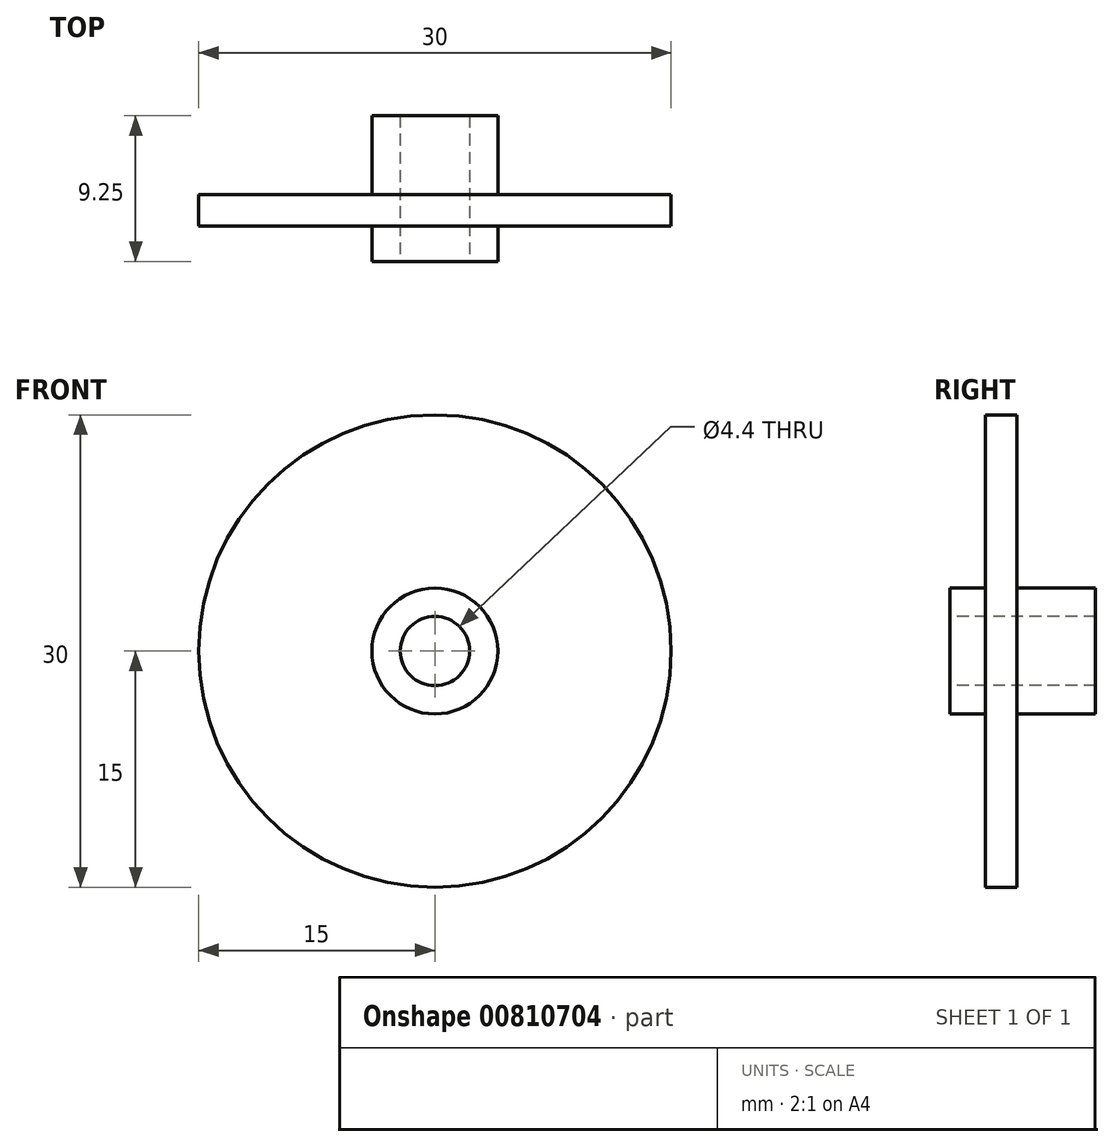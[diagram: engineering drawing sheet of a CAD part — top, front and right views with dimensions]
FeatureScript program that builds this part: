
annotation { "Feature Type Name" : "Feature", "Feature Type Description" : "" }
export const myFeature = defineFeature(function(context is Context, id is Id, definition is map)
    precondition{}
    {
        {
            var Q0;
            Q0=qCreatedBy(makeId("Front.planeOp"),FACE);
            var sketch = newSketch(context, id + "F0", { "sketchPlane" : qUnion([Q0])});
            skCircle(sketch, "E0", {"center": v(0, 0) * mm, "radius": 15 * mm});
            skSolve(sketch);
        }
        {
            var Q0;
            Q0=makeQuery(id+"F0.imprint","IMPRINT",FACE,{"disambiguationData":[TD([[makeQuery(id+"F0.imprint","IMPRINT",EDGE,{"derivedFrom":sQuery(id+"F0.wireOp",EDGE,"E0")}),1.0]])]});
            extrude(context, id + "F1", {"entities" : qUnion([Q0]), "depth" : 2 * mm, "offsetDistance" : 25 * mm});
        }
        {
            var Q0;
            Q0=makeQuery(id+"F1.opExtrude","CAP_FACE",FACE,{"disambiguationData":[OSD([sQuery(id+"F0.wireOp",EDGE,"E0")])],"isStart":false});
            var sketch = newSketch(context, id + "F2", { "sketchPlane" : qUnion([Q0])});
            skCircle(sketch, "E1", {"center": v(0, 0) * mm, "radius": 4 * mm});
            skSolve(sketch);
        }
        {
            var Q0;
            Q0=makeQuery(id+"F2.imprint","IMPRINT",FACE,{"disambiguationData":[TD([[makeQuery(id+"F2.imprint","IMPRINT",EDGE,{"derivedFrom":sQuery(id+"F2.wireOp",EDGE,"E1")}),1.0]])]});
            extrude(context, id + "F3", {"entities" : qUnion([Q0]), "operationType" : NewBodyOperationType.ADD, "depth" : 2.25 * mm, "offsetDistance" : 25 * mm});
        }
        {
            var Q0;
            Q0=makeQuery(id+"F3.opExtrude","CAP_FACE",FACE,{"disambiguationData":[OSD([sQuery(id+"F2.wireOp",EDGE,"E1")])],"isStart":false});
            var sketch = newSketch(context, id + "F4", { "sketchPlane" : qUnion([Q0])});
            skCircle(sketch, "E2", {"center": v(0, 0) * mm, "radius": 2.2 * mm});
            skSolve(sketch);
        }
        {
            var Q0;
            Q0=makeQuery(id+"F4.imprint","IMPRINT",FACE,{"disambiguationData":[TD([[makeQuery(id+"F4.imprint","IMPRINT",EDGE,{"derivedFrom":sQuery(id+"F4.wireOp",EDGE,"E2")}),1.0]])]});
            extrude(context, id + "F5", {"entities" : qUnion([Q0]), "operationType" : NewBodyOperationType.REMOVE, "endBound" : BoundingType.THROUGH_ALL, "oppositeDirection" : true, "depth" : 25 * mm, "offsetDistance" : 25 * mm});
        }
        {
            var Q0;
            Q0=makeQuery(id+"F1.opExtrude","CAP_FACE",FACE,{"disambiguationData":[OSD([sQuery(id+"F0.wireOp",EDGE,"E0")])],"isStart":true});
            var sketch = newSketch(context, id + "F6", { "sketchPlane" : qUnion([Q0])});
            skCircle(sketch, "E3", {"center": v(0, 0) * mm, "radius": 4 * mm});
            skSolve(sketch);
        }
        {
            var Q0;
            Q0=makeQuery(id+"F6.imprint","IMPRINT",FACE,{"disambiguationData":[TD([[makeQuery(id+"F6.imprint","IMPRINT",EDGE,{"derivedFrom":sQuery(id+"F6.wireOp",EDGE,"E3")}),1.0]])]});
            extrude(context, id + "F7", {"entities" : qUnion([Q0]), "operationType" : NewBodyOperationType.ADD, "depth" : 5 * mm, "offsetDistance" : 25 * mm});
        }
    });
